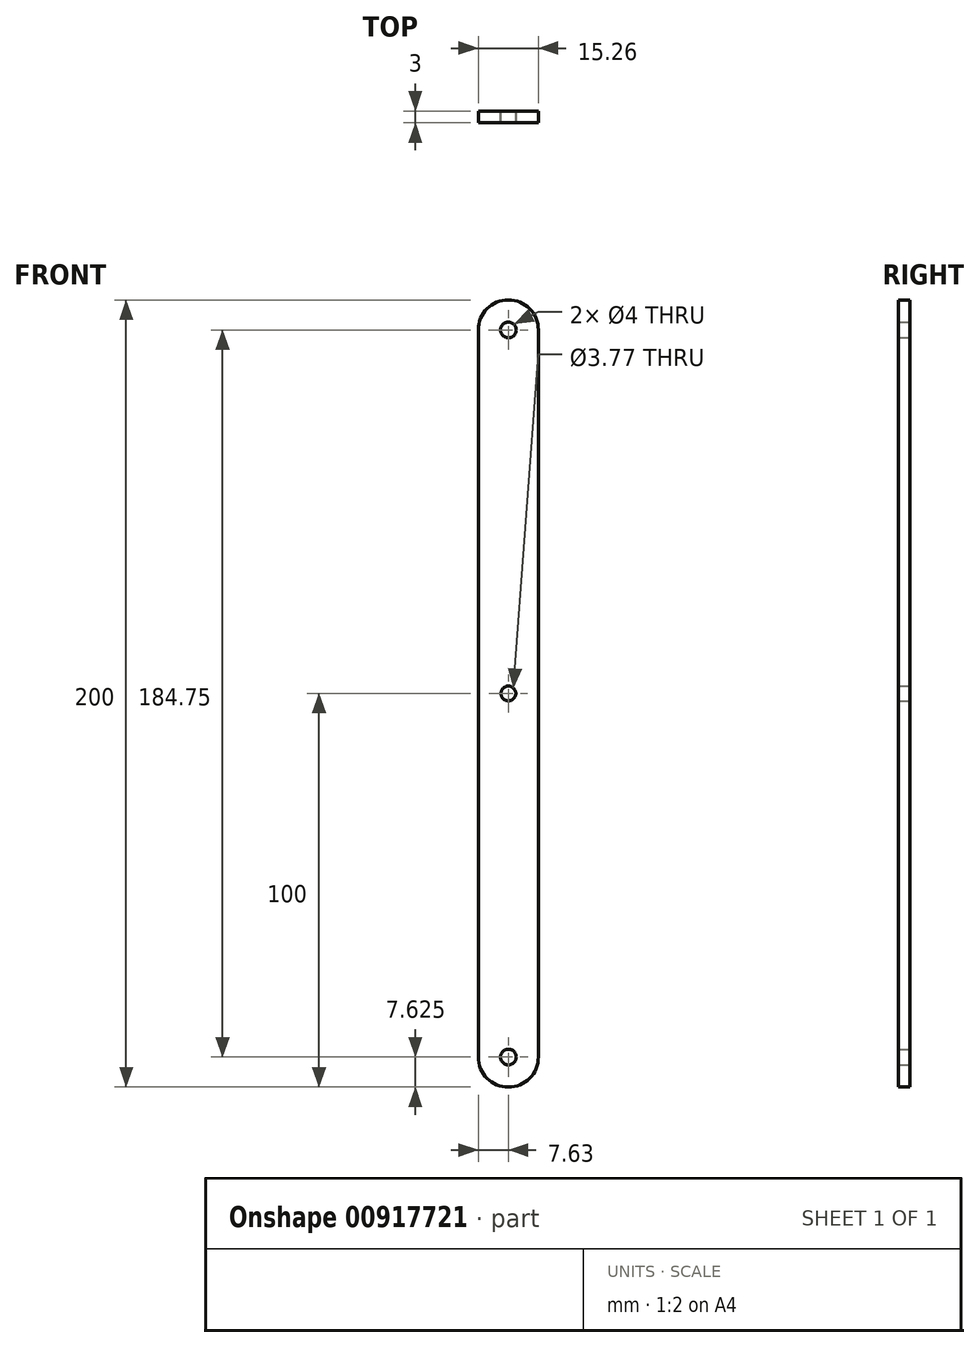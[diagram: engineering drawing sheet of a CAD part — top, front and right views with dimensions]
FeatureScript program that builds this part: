
annotation { "Feature Type Name" : "Feature", "Feature Type Description" : "" }
export const myFeature = defineFeature(function(context is Context, id is Id, definition is map)
    precondition{}
    {
        {
            var Q0;
            Q0=qCreatedBy(makeId("Front.planeOp"),FACE);
            var sketch = newSketch(context, id + "F0", { "sketchPlane" : qUnion([Q0])});
            skLineSegment(sketch, "E0", {"start": v(-7.62, 92.38) * mm, "end": v(-7.62, -92.38) * mm});
            skLineSegment(sketch, "E1", {"start": v(7.63, 92.38) * mm, "end": v(7.63, -92.38) * mm});
            skArc(sketch, "E2", {"start": v(7.63, 92.38) * mm, "mid": v(0, 100) * mm, "end": v(-7.62, 92.38) * mm});
            skArc(sketch, "E3", {"start": v(-7.62, -92.37) * mm, "mid": v(0, -100) * mm, "end": v(7.63, -92.38) * mm});
            skCircle(sketch, "E4", {"center": v(0, 92.38) * mm, "radius": 2 * mm});
            skCircle(sketch, "E5", {"center": v(0, -92.38) * mm, "radius": 2 * mm});
            skLineSegment(sketch, "E6", {"start": v(-7.62, 0) * mm, "end": v(7.63, 0) * mm});
            skLineSegment(sketch, "E7", {"start": v(0, 100) * mm, "end": v(0, 0) * mm});
            skCircle(sketch, "E8", {"center": v(0, 0) * mm, "radius": 1.89 * mm});
            skLineSegment(sketch, "E9", {"start": v(0, -100) * mm, "end": v(0, 0) * mm});
            skSolve(sketch);
        }
        {
            var Q0;
            {var subQ1=sQuery(id+"F0.wireOp",EDGE,"E0");var subQ9=sQuery(id+"F0.wireOp",EDGE,"E2");var subQ10=makeQuery(id+"F0.imprint","INTERSECT",VERTEX,{"derivedFrom":[subQ1,subQ9]});Q0=makeQuery(id+"F0.imprint","IMPRINT",FACE,{"disambiguationData":[TD([[makeQuery(id+"F0.imprint","IMPRINT",EDGE,{"disambiguationData":[TD([[subQ10,-1.0]])],"derivedFrom":subQ1}),1.0]])]});}
            var Q1;
            {var subQ1=sQuery(id+"F0.wireOp",EDGE,"E1");var subQ5=sQuery(id+"F0.wireOp",EDGE,"E2");var subQ6=makeQuery(id+"F0.imprint","INTERSECT",VERTEX,{"derivedFrom":[subQ1,subQ5]});Q1=makeQuery(id+"F0.imprint","IMPRINT",FACE,{"disambiguationData":[TD([[makeQuery(id+"F0.imprint","IMPRINT",EDGE,{"disambiguationData":[TD([[subQ6,-1.0]])],"derivedFrom":subQ1}),-1.0]])]});}
            var Q2;
            {var subQ1=sQuery(id+"F0.wireOp",EDGE,"E0");var subQ5=sQuery(id+"F0.wireOp",EDGE,"E3");var subQ6=makeQuery(id+"F0.imprint","INTERSECT",VERTEX,{"derivedFrom":[subQ1,subQ5]});Q2=makeQuery(id+"F0.imprint","IMPRINT",FACE,{"disambiguationData":[TD([[makeQuery(id+"F0.imprint","IMPRINT",EDGE,{"disambiguationData":[TD([[subQ6,1.0]])],"derivedFrom":subQ1}),1.0]])]});}
            var Q3;
            {var subQ1=sQuery(id+"F0.wireOp",EDGE,"E1");var subQ10=sQuery(id+"F0.wireOp",EDGE,"E3");var subQ11=makeQuery(id+"F0.imprint","INTERSECT",VERTEX,{"derivedFrom":[subQ1,subQ10]});Q3=makeQuery(id+"F0.imprint","IMPRINT",FACE,{"disambiguationData":[TD([[makeQuery(id+"F0.imprint","IMPRINT",EDGE,{"disambiguationData":[TD([[subQ11,1.0]])],"derivedFrom":subQ1}),-1.0]])]});}
            extrude(context, id + "F1", {"entities" : qUnion([Q0, Q1, Q2, Q3]), "depth" : 3 * mm, "offsetDistance" : 25 * mm});
        }
    });
